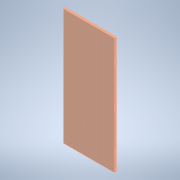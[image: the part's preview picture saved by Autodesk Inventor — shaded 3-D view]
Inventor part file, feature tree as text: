
AUTODESK INVENTOR PART (.ipt)
format: ipt  version: 2021 (Build 250183000, 183)  size: 141,312 bytes
history: native  units: mm
features: extrude x3, sketch x3, pattern_linear x1
ambient origin geometry x8: Origin, YZ Plane, XZ Plane, XY Plane, X Axis, Y Axis, Z Axis, Center Point
bodies: Solid1 (feature_tree)
feature tree (7):
  extrude  "Extrusion1"  Depth=920.0mm
  extrude  "Extrusion2"  Depth=100.0mm
  extrude  "Extrusion3"  Depth=700.0mm
  pattern_linear  "Rectangular Pattern1"  Spacing1=2.5mm  [1 undecoded]
  sketch  "Sketch1"  dims[d0=2100.0mm d1=920.0mm]
  sketch  "Sketch2"  dims[d2=40.0mm d3=0.0mm d4=100.0mm]
  sketch  "Sketch3"  dims[d5=40.0mm d7=30.0mm d9=700.0mm d10=10.0mm d12=10.0mm d14=2.5mm d15=0.0mm d16=8.0mm d17=10.0mm d18=20.0mm d19=5.0mm d20=0.0mm d21=350.0mm d22=20.0mm d24=700.0mm d25=20.0mm d27=700.0mm]
note: 1 required parameter value undecoded (feature->parameter linkage not recoverable at this tier; creation-order binding heuristic only, values carry confidence <= 0.55)
